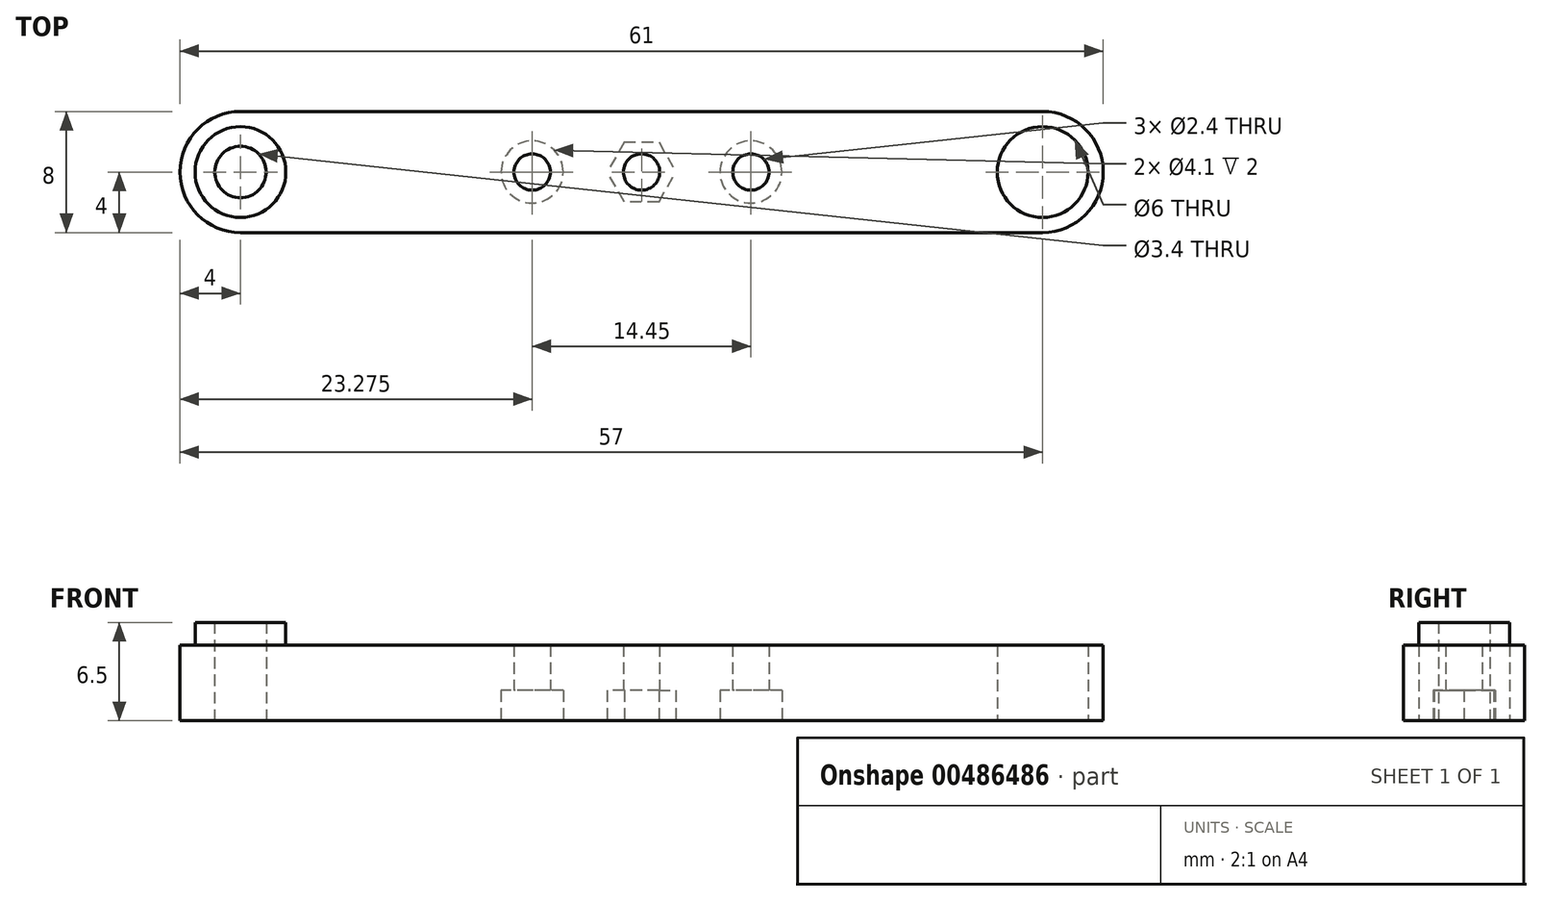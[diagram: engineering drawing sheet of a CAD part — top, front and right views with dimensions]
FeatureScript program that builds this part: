
annotation { "Feature Type Name" : "Feature", "Feature Type Description" : "" }
export const myFeature = defineFeature(function(context is Context, id is Id, definition is map)
    precondition{}
    {
        {
            var Q0;
            Q0=qCreatedBy(makeId("Top.planeOp"),FACE);
            var sketch = newSketch(context, id + "F0", { "sketchPlane" : qUnion([Q0])});
            skCircle(sketch, "E0", {"center": v(-26.5, 38) * mm, "radius": 1.7 * mm});
            skCircle(sketch, "E1.MirrorC", {"center": v(26.5, 38) * mm, "radius": 1.7 * mm});
            skCircle(sketch, "E2.MirrorC", {"center": v(-26.5, -38) * mm, "radius": 1.7 * mm});
            skCircle(sketch, "E3.MirrorC", {"center": v(26.5, -38) * mm, "radius": 1.7 * mm});
            skSolve(sketch);
        }
        {
            var Q0;
            Q0=qCreatedBy(makeId("Top.planeOp"),FACE);
            var sketch = newSketch(context, id + "F1", { "sketchPlane" : qUnion([Q0])});
            skCircle(sketch, "E4", {"center": v(-26.5, 38) * mm, "radius": 3 * mm});
            skCircle(sketch, "E5", {"center": v(-26.5, 38) * mm, "radius": 1.7 * mm});
            skCircle(sketch, "E6.MirrorC", {"center": v(26.5, 38) * mm, "radius": 1.7 * mm});
            skCircle(sketch, "E7.MirrorC", {"center": v(26.5, 38) * mm, "radius": 3 * mm});
            skLineSegment(sketch, "E8.bottom", {"start": v(-30.5, 42) * mm, "end": v(30.5, 42) * mm});
            skLineSegment(sketch, "E8.top", {"start": v(-30.5, 34) * mm, "end": v(30.5, 34) * mm});
            skLineSegment(sketch, "E8.left", {"start": v(-30.5, 42) * mm, "end": v(-30.5, 34) * mm});
            skLineSegment(sketch, "E8.right", {"start": v(30.5, 42) * mm, "end": v(30.5, 34) * mm});
            skSolve(sketch);
        }
        {
            var Q0;
            Q0=makeQuery(id+"F1.imprint","IMPRINT",FACE,{"disambiguationData":[TD([[makeQuery(id+"F1.imprint","IMPRINT",EDGE,{"derivedFrom":sQuery(id+"F1.wireOp",EDGE,"E4")}),-1.0]])]});
            var sketch = newSketch(context, id + "F2", { "sketchPlane" : qUnion([Q0])});
            skLineSegment(sketch, "E9", {"start": v(0, 38) * mm, "end": v(1.44, 35.5) * mm, "construction": true});
            skLineSegment(sketch, "E10", {"start": v(0, 38) * mm, "end": v(0, 36.02) * mm, "construction": true});
            skLineSegment(sketch, "E11", {"start": v(0, 36.02) * mm, "end": v(-1.14, 36.02) * mm});
            skLineSegment(sketch, "E12", {"start": v(-1.14, 36.02) * mm, "end": v(-2.28, 38) * mm});
            skLineSegment(sketch, "E13", {"start": v(-2.28, 38) * mm, "end": v(0, 38) * mm, "construction": true});
            skLineSegment(sketch, "E14.MirrorCS", {"start": v(-1.14, 39.97) * mm, "end": v(-2.28, 38) * mm});
            skLineSegment(sketch, "E15.MirrorCS", {"start": v(0, 39.97) * mm, "end": v(-1.14, 39.97) * mm});
            skLineSegment(sketch, "E16.MirrorCS", {"start": v(0, 36.02) * mm, "end": v(1.14, 36.02) * mm});
            skLineSegment(sketch, "E17.MirrorCS", {"start": v(1.14, 36.02) * mm, "end": v(2.28, 38) * mm});
            skLineSegment(sketch, "E18.MirrorCS", {"start": v(1.14, 39.97) * mm, "end": v(2.28, 38) * mm});
            skLineSegment(sketch, "E19.MirrorCS", {"start": v(0, 39.97) * mm, "end": v(1.14, 39.97) * mm});
            skSolve(sketch);
        }
        {
            var Q0;
            Q0=makeQuery(id+"F2.imprint","IMPRINT",FACE,{"disambiguationData":[TD([[makeQuery(id+"F2.imprint","IMPRINT",EDGE,{"derivedFrom":sQuery(id+"F2.wireOp",EDGE,"E11")}),1.0]])]});
            var sketch = newSketch(context, id + "F3", { "sketchPlane" : qUnion([Q0])});
            skCircle(sketch, "E20", {"center": v(-7.22, 38) * mm, "radius": 2.05 * mm});
            skCircle(sketch, "E21.MirrorC", {"center": v(7.22, 38) * mm, "radius": 2.05 * mm});
            skSolve(sketch);
        }
        {
            var Q0;
            Q0=makeQuery(id+"F1.imprint","IMPRINT",FACE,{"disambiguationData":[TD([[makeQuery(id+"F1.imprint","IMPRINT",EDGE,{"derivedFrom":sQuery(id+"F1.wireOp",EDGE,"E4")}),-1.0]])]});
            var sketch = newSketch(context, id + "F4", { "sketchPlane" : qUnion([Q0])});
            skCircle(sketch, "E22", {"center": v(-7.22, 38) * mm, "radius": 1.2 * mm});
            skCircle(sketch, "E23", {"center": v(0, 38) * mm, "radius": 1.2 * mm});
            skCircle(sketch, "E24.MirrorC", {"center": v(7.22, 38) * mm, "radius": 1.2 * mm});
            skSolve(sketch);
        }
        {
            var Q0;
            Q0=makeQuery(id+"F2.imprint","IMPRINT",FACE,{"disambiguationData":[TD([[makeQuery(id+"F2.imprint","IMPRINT",EDGE,{"derivedFrom":sQuery(id+"F2.wireOp",EDGE,"E11")}),1.0]])]});
            var Q1;
            Q1=makeQuery(id+"F2.imprint","IMPRINT",FACE,{"disambiguationData":[TD([[makeQuery(id+"F2.imprint","IMPRINT",EDGE,{"derivedFrom":sQuery(id+"F2.wireOp",EDGE,"E11")}),-1.0]])]});
            var Q2;
            Q2=makeQuery(id+"F2.imprint","IMPRINT",FACE,{"disambiguationData":[TD([[makeQuery(id+"F2.imprint","IMPRINT",EDGE,{"derivedFrom":makeQuery(id+"F1.imprint","IMPRINT",EDGE,{"derivedFrom":sQuery(id+"F1.wireOp",EDGE,"E4")})}),1.0]])]});
            var Q3;
            Q3=makeQuery(id+"F2.imprint","IMPRINT",FACE,{"disambiguationData":[TD([[makeQuery(id+"F2.imprint","IMPRINT",EDGE,{"derivedFrom":makeQuery(id+"F1.imprint","IMPRINT",EDGE,{"derivedFrom":sQuery(id+"F1.wireOp",EDGE,"E7.MirrorC")})}),-1.0]])]});
            extrude(context, id + "F5", {"entities" : qUnion([Q0, Q1, Q2, Q3]), "depth" : 5 * mm, "offsetDistance" : 25 * mm});
        }
        {
            var Q0;
            Q0=makeQuery(id+"F1.imprint","IMPRINT",FACE,{"disambiguationData":[TD([[makeQuery(id+"F1.imprint","IMPRINT",EDGE,{"derivedFrom":sQuery(id+"F1.wireOp",EDGE,"E4")}),1.0]])]});
            var Q1;
            Q1=makeQuery(id+"F1.imprint","IMPRINT",FACE,{"disambiguationData":[TD([[makeQuery(id+"F1.imprint","IMPRINT",EDGE,{"derivedFrom":sQuery(id+"F1.wireOp",EDGE,"E6.MirrorC")}),1.0]])]});
            extrude(context, id + "F6", {"entities" : qUnion([Q0, Q1]), "operationType" : NewBodyOperationType.ADD, "depth" : 6.5 * mm, "offsetDistance" : 25 * mm});
        }
        {
            var Q0;
            Q0=qSketchRegion(id+"F0",true);
            extrude(context, id + "F7", {"entities" : qUnion([Q0]), "operationType" : NewBodyOperationType.REMOVE, "oppositeDirection" : true, "depth" : 25 * mm, "offsetDistance" : 25 * mm, "symmetric" : true});
        }
        {
            var Q0;
            Q0=qSketchRegion(id+"F3",true);
            var Q1;
            Q1=sQuery(id+"F3.wireOp",EDGE,"E20");
            var Q2;
            Q2=sQuery(id+"F3.wireOp",EDGE,"E21.MirrorC");
            extrude(context, id + "F8", {"entities" : qUnion([Q0]), "operationType" : NewBodyOperationType.REMOVE, "surfaceEntities" : qUnion([Q1, Q2]), "depth" : 2 * mm, "offsetDistance" : 25 * mm});
        }
        {
            var Q0;
            Q0=qSketchRegion(id+"F2",true);
            extrude(context, id + "F9", {"entities" : qUnion([Q0]), "operationType" : NewBodyOperationType.REMOVE, "depth" : 2 * mm, "offsetDistance" : 25 * mm});
        }
        {
            var Q0;
            Q0=makeQuery(id+"F5.opExtrude","SWEPT_EDGE",EDGE,{"disambiguationData":[OSD([sQuery(id+"F1.wireOp",EDGE,"E8.bottom"),sQuery(id+"F1.wireOp",EDGE,"E8.left")])]});
            var Q1;
            Q1=makeQuery(id+"F5.opExtrude","SWEPT_EDGE",EDGE,{"disambiguationData":[OSD([sQuery(id+"F1.wireOp",EDGE,"E8.top"),sQuery(id+"F1.wireOp",EDGE,"E8.left")])]});
            var Q2;
            Q2=makeQuery(id+"F5.opExtrude","SWEPT_EDGE",EDGE,{"disambiguationData":[OSD([sQuery(id+"F1.wireOp",EDGE,"E8.bottom"),sQuery(id+"F1.wireOp",EDGE,"E8.right")])]});
            var Q3;
            Q3=makeQuery(id+"F5.opExtrude","SWEPT_EDGE",EDGE,{"disambiguationData":[OSD([sQuery(id+"F1.wireOp",EDGE,"E8.top"),sQuery(id+"F1.wireOp",EDGE,"E8.right")])]});
            fillet(context, id + "F10", {"entities" : qUnion([Q0, Q1, Q2, Q3]), "radius" : 4 * mm, "tangentPropagation" : true, "allowEdgeOverflow" : false});
        }
        {
            var Q0;
            Q0=qSketchRegion(id+"F4",true);
            extrude(context, id + "F11", {"entities" : qUnion([Q0]), "operationType" : NewBodyOperationType.REMOVE, "endBound" : BoundingType.THROUGH_ALL, "depth" : 25 * mm, "offsetDistance" : 25 * mm});
        }
    });
